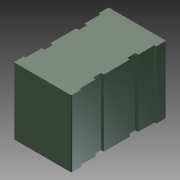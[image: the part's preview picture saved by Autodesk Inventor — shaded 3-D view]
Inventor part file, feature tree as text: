
AUTODESK INVENTOR PART (.ipt)
format: ipt  version: 2014 (Build 180170000, 170)  size: 157,184 bytes
history: native  units: in
note: dims shown in document units (in); Inventor stores cm internally (conversion verified against a paired STEP export)
features: other x21, extrude x3, sketch x3, pattern_linear x1
ambient origin geometry x8: Origin, YZ Plane, XZ Plane, XY Plane, X Axis, Y Axis, Z Axis, Center Point
bodies: Solid1 (feature_tree)
feature tree (28):
  extrude  "Extrusion1"  Depth=0.001in TaperAngle=0.0deg
  extrude  "Extrusion2"  Depth=0.185in TaperAngle=0.0deg
  extrude  "Extrusion3"  [1 undecoded]
  pattern_linear  "Rectangular Pattern1"  [2 undecoded]
  other  "rot_XY"
  other  "rot_YZ"
  other  "rot_ZX"
  other  "rot_X"
  other  "rot_Y"
  other  "rot_Z"
  other  "rot_Center"
  other  "to_cover_XY"
  other  "to_cover_YZ"
  other  "to_cover_ZX"
  other  "to_cover_X"
  other  "to_cover_Y"
  other  "to_cover_Z"
  other  "to_cover_Center"
  other  "to_terminals_XY"
  other  "to_terminals_YZ"
  other  "to_terminals_ZX"
  other  "to_terminals_X"
  other  "to_terminals_Y"
  other  "to_terminals_Z"
  other  "to_terminals_Center"
  sketch  "Sketch_2"  dims[d4=0.01in d5=0.0in d6=0.7874in d8=0.185in d9=0.3937in d11=0.0in]
  sketch  "Sketch_1"  dims[d0=0.361in d1=0.0in d2=0.001in d3=0.0in]
  sketch  "Sketch_7"
note: 3 required parameter values undecoded (feature->parameter linkage not recoverable at this tier; creation-order binding heuristic only, values carry confidence <= 0.55)
